# Revit family: 1.rvt
name_source: partatom
category: Pipe Accessories
revit_build: Autodesk Revit 2018 (Build: 20190510_1515(x64)
units: mm (PartAtom-declared; Revit-internal decimal feet)

## family parameters
Always vertical = No
Cut with Voids When Loaded = No
OmniClass Number = 23.65.00.00
OmniClass Title = Supply and Distribution of Liquids and Gases
Part Type = Normal
Round Connector Dimension = Use Diameter
Shared = No
Work Plane-Based = No

## types (2) — shared parameters
Antifreeze: = Passiveted Propylene Glycol
Application fluids = Water or glycol solutions
BIMobject category = HVAC: Other HVAC
Body Material = Pintossi - Metal - Brass CW617N
Brand url = http://www.pintossi.it
Conditioning: = as indicated by the producer
Copper (CU): = < 0,1 mg/kg (< 0,05 mg/kg for steam)
Description = Pintossi+C motorized zone valves are the perfect solution to be used when a thermal regulation divided in more enviroments is needed, connecting the valve to a room thermostat, giving the information of opening/closing, depending on the set temperature.

Pintossi+C zone valves garantuee high performance levels: reduced dimensions and ease of use during installation allow to automatically intercept the fluid in hydraulic water systems and zone heating systems.

Besides the valve is equipped with APS (Anti-locking Pintossi System) a unique patented mechanism which prevent the opening and closing operation locking caused by dirt and limescale.

3 ways motorized zone valve can be used in traditional heating system to divert the flow back or to switch from summer to winter mode, to use the system to heat up or cool down the room.

All the valves are equipped with pipe unions for an easy installtion.

Main features:

- No seepage

- Short opening and closing times

- Operational capacity with high differential pressures

- Low head losses thanks to the full bore flow

- Match with any type of 3-contact controls

The valve can be easily motorized using Pintossi+C actuator art.770 that can be used even with manual option.
Design country = Italy
Edition number = 1
Fluid aspect: = Limpid
IFC Classification = Valve
Iron (FE): = < 0,5 mg/kg (< 0,1 mg/kg for steam)
Manufacturer = Pintossi+c
Manufacturer name = Pintossi+c
Masterformat 2014 Code = 23 00 00
Masterformat 2014 Description = Heating, Ventilating and Air Conditioning (HVAC)
Material main = Brass
Maximum percentage of glycol [%] = 30
Maximum working pressure = 1000000.0 Pa
Maximum working temperature = 110 °C
Model = 773
NBS Reference Code = 94
NBS Reference Description = Valves
OmniClass Code = 23-27 31 00
OmniClass Description = Valves
PH: = Between 7 and 8Between 7 and 8
Product Guid = 33698341-e965-4c2e-ad69-203d5952db6d
Product data url = https://www.bimobject.com
Product family = Zone valves
Product group = Ball zone valves
Protection level = 90.00°
Rotation angle = -10÷55°C
Torque = 800 mm  [stored 2.62467 ft]
UNSPSC Code = 401416
URL = www.pintossi.it
Uniclass 1.4 Code = L7136
Uniclass 1.4 Description = Valves
Uniclass 2.0 Code = PR-94
Uniclass 2.0 Description = Valves
Uniclass 2015 Code = Ss_60
Uniclass 2015 Name = Heating, cooling and refrigeration systems
Uniformat II Code = D30
Uniformat II Description = HVAC
Voltage = 230 V

## per-type parameters (varying)
| type | Conector Length | G | Main Inlet/Outlet Diameter | Main Inlet/Outlet Radius | Mainfold Length | Radius Outer |
| 1" - 3 ways | 75 mm | 15 mm  [stored 0.0492126 ft] | 25 mm  [stored 0.082021 ft] | 13 mm  [stored 0.0426509 ft] | 145 mm  [stored 0.475722 ft] | 17 mm |
| 3/4" - 3 ways | 70 mm  [stored 0.229659 ft] | 12 mm  [stored 0.0393701 ft] | 19 mm | 10 mm  [stored 0.0328084 ft] | 135 mm  [stored 0.442913 ft] | 13 mm  [stored 0.0426509 ft] |

note: [stored X ft] marks values corroborated as IEEE doubles in the binary element streams (Revit-internal decimal feet)

## geometry (parser evidence)
native form markers: Sweep x3
no freeform markers — native parametric forms only
